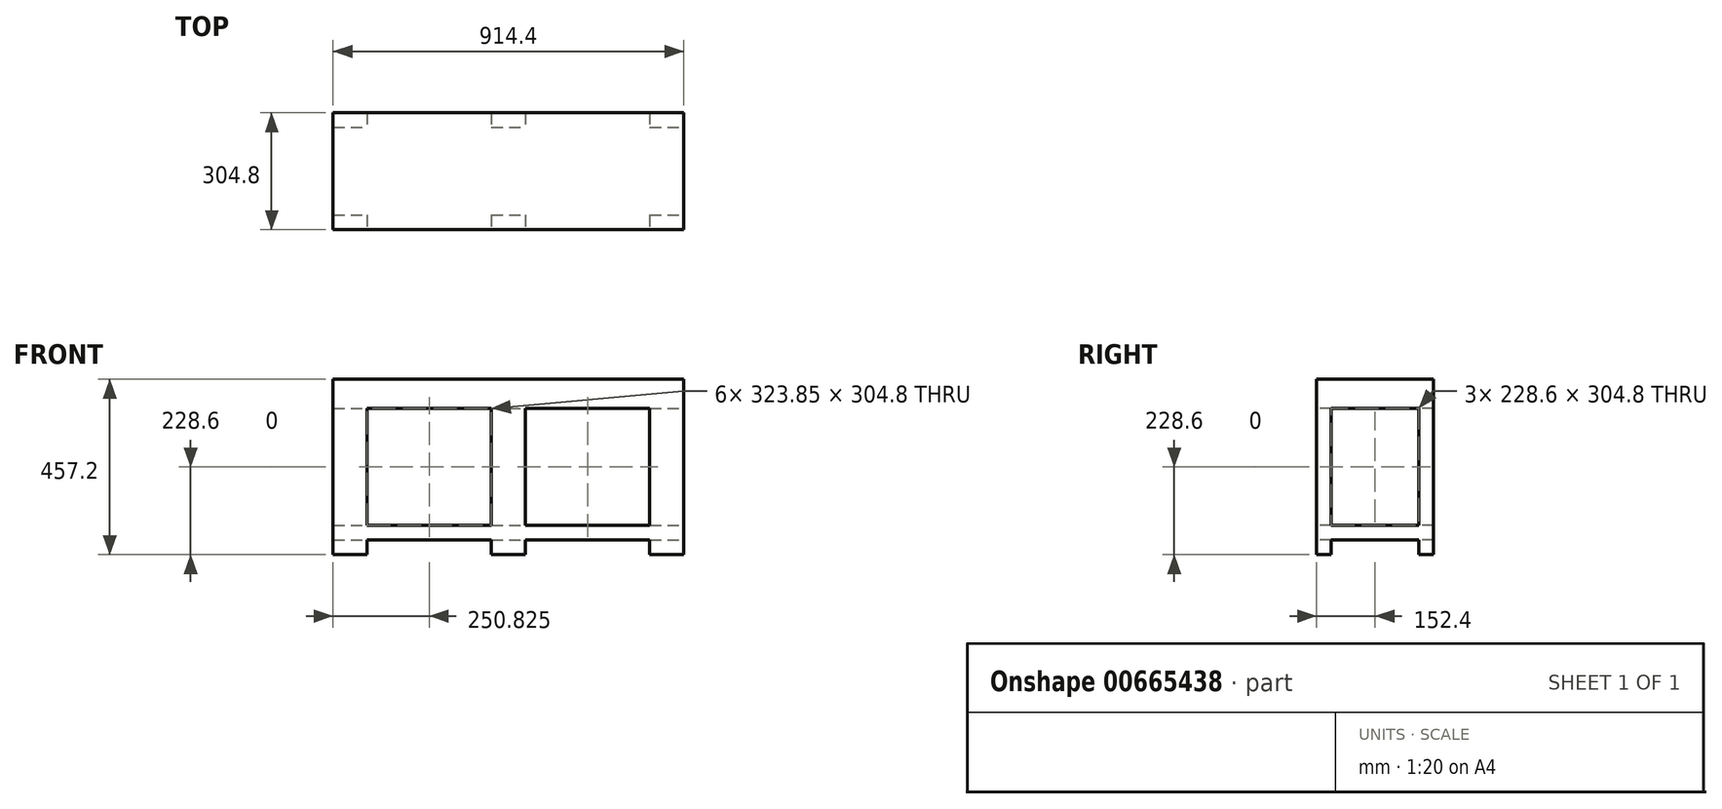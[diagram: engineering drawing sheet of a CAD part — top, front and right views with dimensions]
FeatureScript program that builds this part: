
annotation { "Feature Type Name" : "Feature", "Feature Type Description" : "" }
export const myFeature = defineFeature(function(context is Context, id is Id, definition is map)
    precondition{}
    {
        {
            var Q0;
            Q0=qCreatedBy(makeId("Top.planeOp"),FACE);
            var sketch = newSketch(context, id + "F0", { "sketchPlane" : qUnion([Q0])});
            skLineSegment(sketch, "E0.bottom", {"start": v(457.2, -152.4) * mm, "end": v(-457.2, -152.4) * mm});
            skLineSegment(sketch, "E0.top", {"start": v(457.2, 152.4) * mm, "end": v(-457.2, 152.4) * mm});
            skLineSegment(sketch, "E0.left", {"start": v(457.2, -152.4) * mm, "end": v(457.2, 152.4) * mm});
            skLineSegment(sketch, "E0.right", {"start": v(-457.2, -152.4) * mm, "end": v(-457.2, 152.4) * mm});
            skPoint(sketch, "E0.middle", {"position": v(0, 0) * mm});
            skSolve(sketch);
        }
        {
            var Q0;
            Q0 = qSketchRegion(id + "F0", true);
            extrude(context, id + "F1", {"entities" : qUnion([Q0]), "depth" : 457.2 * mm, "offsetDistance" : 25.4 * mm});
        }
        {
            var Q0;
            Q0=makeQuery(id+"F1.opExtrude","SWEPT_FACE",FACE,{"disambiguationData":[OSD([sQuery(id+"F0.wireOp",EDGE,"E0.bottom")])]});
            var sketch = newSketch(context, id + "F2", { "sketchPlane" : qUnion([Q0])});
            skLineSegment(sketch, "E1", {"start": v(0, 0) * mm, "end": v(0, 712.52) * mm, "construction": true});
            skLineSegment(sketch, "E2.bottom", {"start": v(-368.3, 76.2) * mm, "end": v(-44.45, 76.2) * mm});
            skLineSegment(sketch, "E2.top", {"start": v(-368.3, 381) * mm, "end": v(-44.45, 381) * mm});
            skLineSegment(sketch, "E2.left", {"start": v(-368.3, 76.2) * mm, "end": v(-368.3, 381) * mm});
            skLineSegment(sketch, "E2.right", {"start": v(-44.45, 76.2) * mm, "end": v(-44.45, 381) * mm});
            skLineSegment(sketch, "E3.MirrorCS", {"start": v(368.3, 381) * mm, "end": v(44.45, 381) * mm});
            skLineSegment(sketch, "E4.MirrorCS", {"start": v(44.45, 76.2) * mm, "end": v(44.45, 381) * mm});
            skLineSegment(sketch, "E5.MirrorCS", {"start": v(368.3, 76.2) * mm, "end": v(44.45, 76.2) * mm});
            skLineSegment(sketch, "E6.MirrorCS", {"start": v(368.3, 76.2) * mm, "end": v(368.3, 381) * mm});
            skSolve(sketch);
        }
        {
            var Q0;
            Q0 = qSketchRegion(id + "F2", true);
            extrude(context, id + "F3", {"entities" : qUnion([Q0]), "operationType" : NewBodyOperationType.REMOVE, "endBound" : BoundingType.THROUGH_ALL, "oppositeDirection" : true, "depth" : 25.4 * mm, "offsetDistance" : 25.4 * mm});
        }
        {
            var Q0;
            Q0=makeQuery(id+"F1.opExtrude","SWEPT_FACE",FACE,{"disambiguationData":[OSD([sQuery(id+"F0.wireOp",EDGE,"E0.left")])]});
            var sketch = newSketch(context, id + "F4", { "sketchPlane" : qUnion([Q0])});
            skLineSegment(sketch, "E7.bottom", {"start": v(-114.3, 76.2) * mm, "end": v(114.3, 76.2) * mm});
            skLineSegment(sketch, "E7.top", {"start": v(-114.3, 381) * mm, "end": v(114.3, 381) * mm});
            skLineSegment(sketch, "E7.left", {"start": v(-114.3, 76.2) * mm, "end": v(-114.3, 381) * mm});
            skLineSegment(sketch, "E7.right", {"start": v(114.3, 76.2) * mm, "end": v(114.3, 381) * mm});
            skSolve(sketch);
        }
        {
            var Q0;
            Q0 = qSketchRegion(id + "F4", true);
            extrude(context, id + "F5", {"entities" : qUnion([Q0]), "operationType" : NewBodyOperationType.REMOVE, "endBound" : BoundingType.THROUGH_ALL, "oppositeDirection" : true, "depth" : 25.4 * mm, "offsetDistance" : 25.4 * mm});
        }
        {
            var Q0;
            Q0=makeQuery(id+"F1.opExtrude","SWEPT_FACE",FACE,{"disambiguationData":[OSD([sQuery(id+"F0.wireOp",EDGE,"E0.bottom")])]});
            var sketch = newSketch(context, id + "F6", { "sketchPlane" : qUnion([Q0])});
            skLineSegment(sketch, "E8.bottom", {"start": v(-368.3, 0) * mm, "end": v(-44.45, 0) * mm});
            skLineSegment(sketch, "E8.top", {"start": v(-368.3, 38.1) * mm, "end": v(-44.45, 38.1) * mm});
            skLineSegment(sketch, "E8.left", {"start": v(-368.3, 0) * mm, "end": v(-368.3, 38.1) * mm});
            skLineSegment(sketch, "E8.right", {"start": v(-44.45, 0) * mm, "end": v(-44.45, 38.1) * mm});
            skLineSegment(sketch, "E9.bottom", {"start": v(368.3, 0) * mm, "end": v(44.45, 0) * mm});
            skLineSegment(sketch, "E9.top", {"start": v(368.3, 38.1) * mm, "end": v(44.45, 38.1) * mm});
            skLineSegment(sketch, "E9.left", {"start": v(368.3, 0) * mm, "end": v(368.3, 38.1) * mm});
            skLineSegment(sketch, "E9.right", {"start": v(44.45, 0) * mm, "end": v(44.45, 38.1) * mm});
            skSolve(sketch);
        }
        {
            var Q0;
            Q0 = qSketchRegion(id + "F6", true);
            extrude(context, id + "F7", {"entities" : qUnion([Q0]), "operationType" : NewBodyOperationType.REMOVE, "endBound" : BoundingType.THROUGH_ALL, "oppositeDirection" : true, "depth" : 25.4 * mm, "offsetDistance" : 25.4 * mm});
        }
        {
            var Q0;
            Q0=makeQuery(id+"F1.opExtrude","SWEPT_FACE",FACE,{"disambiguationData":[OSD([sQuery(id+"F0.wireOp",EDGE,"E0.left")])]});
            var sketch = newSketch(context, id + "F8", { "sketchPlane" : qUnion([Q0])});
            skLineSegment(sketch, "E10.bottom", {"start": v(-114.3, 0) * mm, "end": v(114.3, 0) * mm});
            skLineSegment(sketch, "E10.top", {"start": v(-114.3, 38.1) * mm, "end": v(114.3, 38.1) * mm});
            skLineSegment(sketch, "E10.left", {"start": v(-114.3, 0) * mm, "end": v(-114.3, 38.1) * mm});
            skLineSegment(sketch, "E10.right", {"start": v(114.3, 0) * mm, "end": v(114.3, 38.1) * mm});
            skSolve(sketch);
        }
        {
            var Q0;
            Q0 = qSketchRegion(id + "F8", true);
            extrude(context, id + "F9", {"entities" : qUnion([Q0]), "operationType" : NewBodyOperationType.REMOVE, "endBound" : BoundingType.THROUGH_ALL, "oppositeDirection" : true, "depth" : 25.4 * mm, "offsetDistance" : 25.4 * mm});
        }
    });
